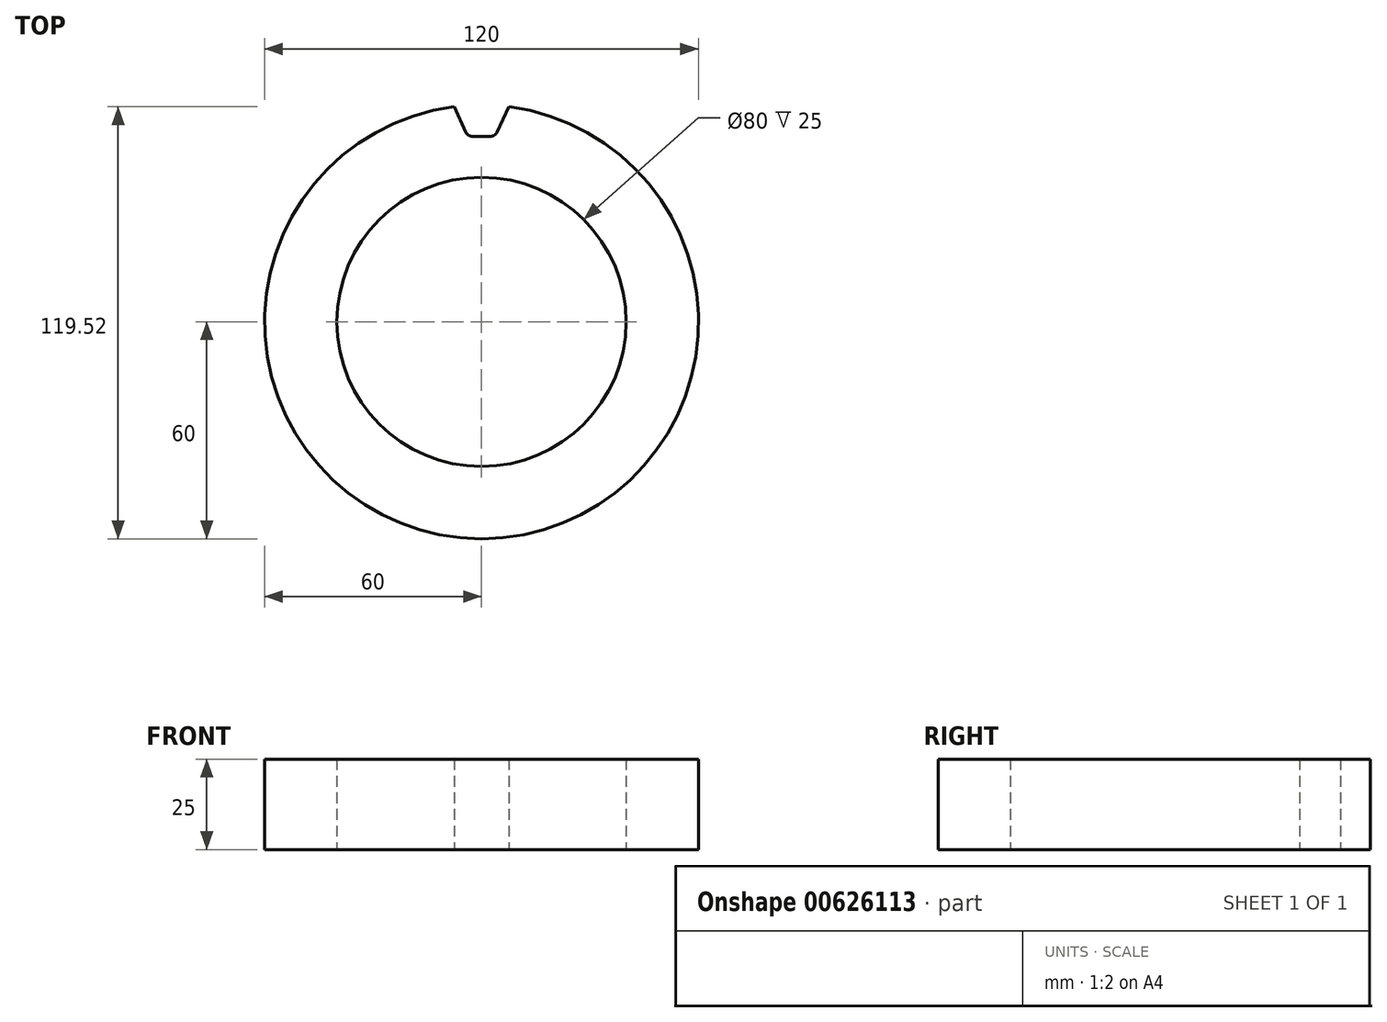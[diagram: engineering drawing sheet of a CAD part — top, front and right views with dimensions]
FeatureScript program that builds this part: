
annotation { "Feature Type Name" : "Feature", "Feature Type Description" : "" }
export const myFeature = defineFeature(function(context is Context, id is Id, definition is map)
    precondition{}
    {
        {
            var Q0;
            Q0=qCreatedBy(makeId("Top.planeOp"),FACE);
            var sketch = newSketch(context, id + "F0", { "sketchPlane" : qUnion([Q0])});
            skCircle(sketch, "E0", {"center": v(0, 0) * mm, "radius": 40 * mm});
            skCircle(sketch, "E1.0", {"center": v(0, 0) * mm, "radius": 60 * mm});
            skSolve(sketch);
        }
        {
            var Q0;
            Q0=makeQuery(id+"F0.imprint","IMPRINT",FACE,{"disambiguationData":[TD([[makeQuery(id+"F0.imprint","IMPRINT",EDGE,{"derivedFrom":sQuery(id+"F0.wireOp",EDGE,"E0")}),-1.0]])]});
            extrude(context, id + "F1", {"entities" : qUnion([Q0]), "depth" : 25 * mm, "offsetDistance" : 25 * mm});
        }
        {
            var Q0;
            Q0=makeQuery(id+"F1.opExtrude","CAP_FACE",FACE,{"disambiguationData":[OSD([sQuery(id+"F0.wireOp",EDGE,"E0"),sQuery(id+"F0.wireOp",EDGE,"E1.0")])],"isStart":true});
            var sketch = newSketch(context, id + "F2", { "sketchPlane" : qUnion([Q0])});
            skLineSegment(sketch, "E2", {"start": v(0, -60) * mm, "end": v(-3.07, -69.52) * mm});
            skLineSegment(sketch, "E3", {"start": v(-22.3, -65.7) * mm, "end": v(-22.3, -55.7) * mm});
            skArc(sketch, "E4", {"start": v(-22.3, -65.7) * mm, "mid": v(-14.25, -75.5) * mm, "end": v(-3.07, -69.52) * mm});
            skSolve(sketch);
        }
        {
            var Q0;
            Q0=qCreatedBy(makeId("Top.planeOp"),FACE);
            var sketch = newSketch(context, id + "F3", { "sketchPlane" : qUnion([Q0])});
            skLineSegment(sketch, "E5", {"start": v(0, 72.35) * mm, "end": v(0, 0) * mm, "construction": true});
            skLineSegment(sketch, "E6", {"start": v(-7.59, 59.52) * mm, "end": v(-4.31, 52.5) * mm});
            skLineSegment(sketch, "E7", {"start": v(-2.5, 51.34) * mm, "end": v(2.5, 51.34) * mm});
            skLineSegment(sketch, "E8", {"start": v(4.31, 52.5) * mm, "end": v(7.59, 59.52) * mm});
            skPoint(sketch, "E9.visualSharp", {"position": v(-3.77, 51.34) * mm});
            skArc(sketch, "E9.filletArc", {"start": v(-4.31, 52.5) * mm, "mid": v(-3.57, 51.65) * mm, "end": v(-2.5, 51.34) * mm});
            skPoint(sketch, "E10.visualSharp", {"position": v(3.77, 51.34) * mm});
            skArc(sketch, "E10.filletArc", {"start": v(2.5, 51.34) * mm, "mid": v(3.57, 51.65) * mm, "end": v(4.31, 52.5) * mm});
            skArc(sketch, "E11", {"start": v(7.59, 59.52) * mm, "mid": v(0, 60.22) * mm, "end": v(-7.59, 59.52) * mm});
            skSolve(sketch);
        }
        {
            var Q0;
            Q0=makeQuery(id+"F3.imprint","IMPRINT",FACE,{"disambiguationData":[TD([[makeQuery(id+"F3.imprint","IMPRINT",EDGE,{"derivedFrom":sQuery(id+"F3.wireOp",EDGE,"E6")}),1.0]])]});
            var Q1;
            {var subQ0=sQuery(id+"F2.wireOp",EDGE,"E2");Q1=makeQuery(id+"F2.imprint","IMPRINT",FACE,{"disambiguationData":[TD([[makeQuery(id+"F2.imprint","IMPRINT",EDGE,{"derivedFrom":subQ0}),-1.0]])]});}
            extrude(context, id + "F4", {"entities" : qUnion([Q0, Q1]), "operationType" : NewBodyOperationType.REMOVE, "endBound" : BoundingType.THROUGH_ALL, "depth" : 25 * mm, "offsetDistance" : 25 * mm});
        }
    });
